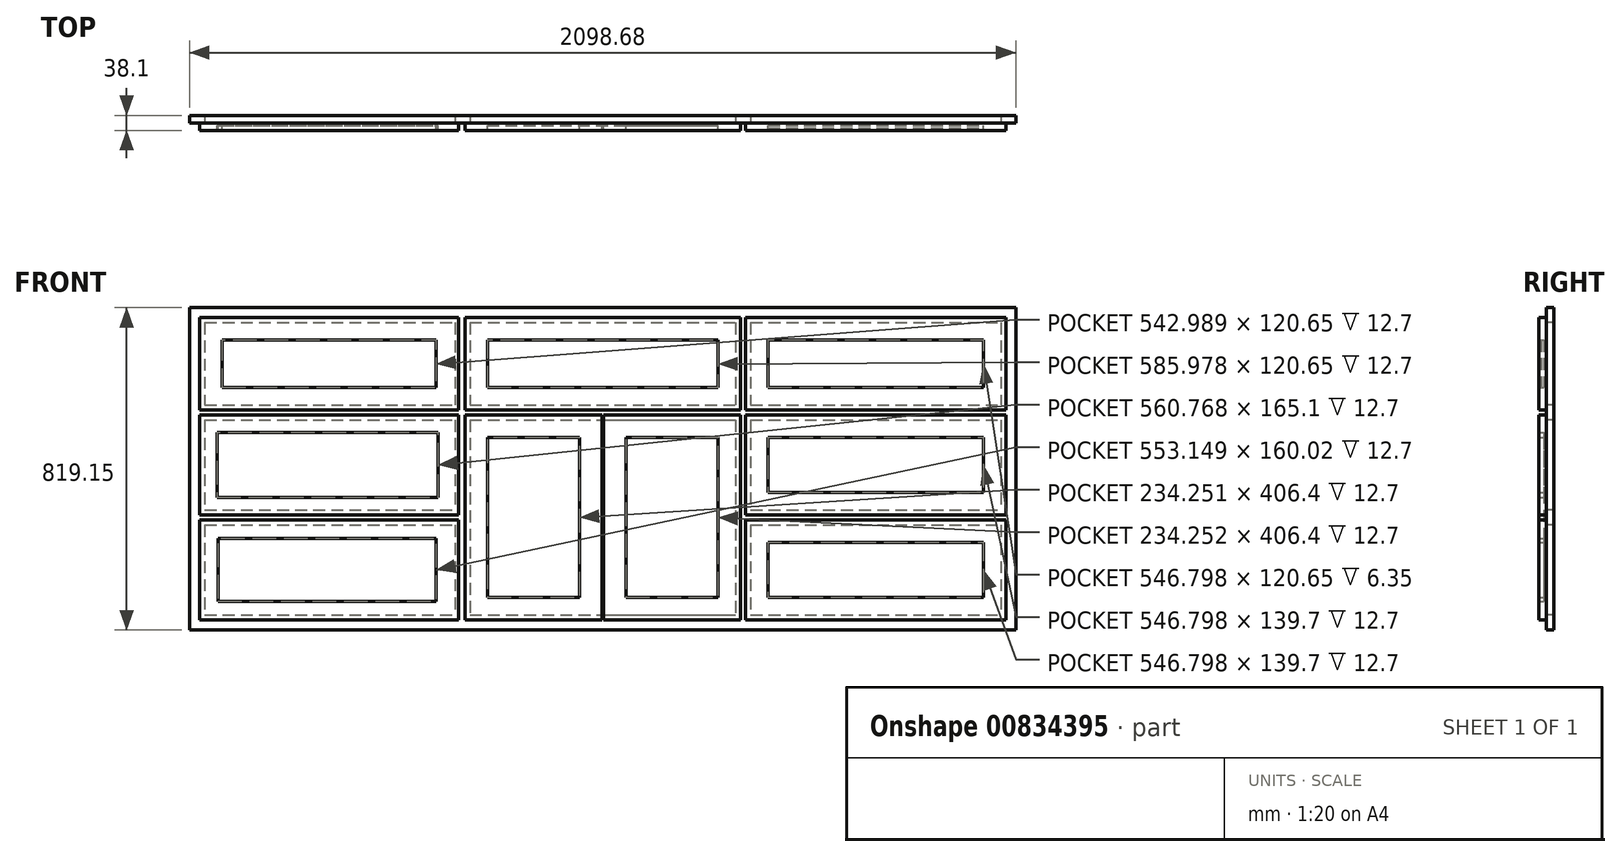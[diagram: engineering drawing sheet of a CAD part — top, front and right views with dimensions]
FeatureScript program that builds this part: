
annotation { "Feature Type Name" : "Feature", "Feature Type Description" : "" }
export const myFeature = defineFeature(function(context is Context, id is Id, definition is map)
    precondition{}
    {
        {
            var Q0;
            Q0=qCreatedBy(makeId("Front.planeOp"),FACE);
            var sketch = newSketch(context, id + "F0", { "sketchPlane" : qUnion([Q0])});
            skLineSegment(sketch, "E0.bottom", {"start": v(-1024.55, 548.46) * mm, "end": v(-350.75, 548.46) * mm});
            skLineSegment(sketch, "E0.left", {"start": v(-1024.55, 548.46) * mm, "end": v(-1024.55, -270.7) * mm});
            skLineSegment(sketch, "E0.right", {"start": v(1074.13, 548.46) * mm, "end": v(1074.13, -270.7) * mm});
            skLineSegment(sketch, "E1.0", {"start": v(-1024.55, -270.7) * mm, "end": v(-350.75, -270.7) * mm});
            skLineSegment(sketch, "E2", {"start": v(24.79, 721.9) * mm, "end": v(24.79, -476.43) * mm, "construction": true});
            skPoint(sketch, "E2.startSnap0", {"position": v(24.79, 548.46) * mm});
            skLineSegment(sketch, "E3.0", {"start": v(-986.45, -232.6) * mm, "end": v(-350.75, -232.6) * mm});
            skLineSegment(sketch, "E4.0", {"start": v(-986.45, 548.46) * mm, "end": v(-986.45, -270.7) * mm});
            skLineSegment(sketch, "E5.0", {"start": v(1036.03, 548.46) * mm, "end": v(1036.03, -270.7) * mm});
            skLineSegment(sketch, "E6.0", {"start": v(-986.45, 510.36) * mm, "end": v(-350.75, 510.36) * mm});
            skLineSegment(sketch, "E7", {"start": v(362.23, 548.46) * mm, "end": v(362.23, -270.7) * mm});
            skLineSegment(sketch, "E8.MirrorCS", {"start": v(-312.65, 548.46) * mm, "end": v(-312.65, -270.7) * mm});
            skLineSegment(sketch, "E9.0", {"start": v(400.33, 548.46) * mm, "end": v(400.33, -270.7) * mm});
            skLineSegment(sketch, "E10.0", {"start": v(-350.75, 548.46) * mm, "end": v(-350.75, -270.7) * mm});
            skLineSegment(sketch, "E11.trimOffspring", {"start": v(-312.65, 510.36) * mm, "end": v(362.23, 510.36) * mm});
            skLineSegment(sketch, "E12.trimOffspring", {"start": v(-312.65, 548.46) * mm, "end": v(362.23, 548.46) * mm});
            skLineSegment(sketch, "E13", {"start": v(-350.75, 548.46) * mm, "end": v(-312.65, 548.46) * mm});
            skLineSegment(sketch, "E14.trimOffspring", {"start": v(-312.65, -232.6) * mm, "end": v(362.23, -232.6) * mm});
            skLineSegment(sketch, "E15.trimOffspring", {"start": v(-312.65, -270.7) * mm, "end": v(362.23, -270.7) * mm});
            skLineSegment(sketch, "E16", {"start": v(-350.75, -270.7) * mm, "end": v(-312.65, -270.7) * mm});
            skLineSegment(sketch, "E17.trimOffspring", {"start": v(400.33, -232.6) * mm, "end": v(1036.03, -232.6) * mm});
            skLineSegment(sketch, "E18.trimOffspring", {"start": v(400.33, -270.7) * mm, "end": v(1074.13, -270.7) * mm});
            skLineSegment(sketch, "E19", {"start": v(362.23, -270.7) * mm, "end": v(400.33, -270.7) * mm});
            skLineSegment(sketch, "E20.trimOffspring", {"start": v(400.33, 548.46) * mm, "end": v(1074.13, 548.46) * mm});
            skLineSegment(sketch, "E21.trimOffspring", {"start": v(400.33, 510.36) * mm, "end": v(1036.03, 510.36) * mm});
            skLineSegment(sketch, "E22", {"start": v(362.23, 548.46) * mm, "end": v(400.33, 548.46) * mm});
            skLineSegment(sketch, "E23", {"start": v(-986.45, 138.88) * mm, "end": v(1036.03, 138.88) * mm, "construction": true});
            skLineSegment(sketch, "E24.0", {"start": v(-986.45, -4) * mm, "end": v(-350.75, -4) * mm});
            skLineSegment(sketch, "E25.0", {"start": v(400.33, -4) * mm, "end": v(1036.03, -4) * mm});
            skLineSegment(sketch, "E26.0", {"start": v(-986.45, 262.7) * mm, "end": v(-350.75, 262.7) * mm});
            skLineSegment(sketch, "E27.0", {"start": v(-986.45, 300.8) * mm, "end": v(-350.75, 300.8) * mm});
            skLineSegment(sketch, "E28", {"start": v(-986.45, 34.1) * mm, "end": v(-350.75, 34.1) * mm});
            skLineSegment(sketch, "E29", {"start": v(400.33, 34.1) * mm, "end": v(1036.03, 34.1) * mm});
            skLineSegment(sketch, "E30.bottom", {"start": v(-1024.55, -270.7) * mm, "end": v(1074.13, -270.7) * mm});
            skLineSegment(sketch, "E30.top", {"start": v(-1024.55, -346.9) * mm, "end": v(1074.13, -346.9) * mm});
            skLineSegment(sketch, "E30.left", {"start": v(-1024.55, -270.7) * mm, "end": v(-1024.55, -346.9) * mm});
            skLineSegment(sketch, "E30.right", {"start": v(1074.13, -270.7) * mm, "end": v(1074.13, -346.9) * mm});
            skLineSegment(sketch, "E31.trimOffspring", {"start": v(-312.65, 300.8) * mm, "end": v(362.23, 300.8) * mm});
            skLineSegment(sketch, "E32.trimOffspring", {"start": v(-312.65, 262.7) * mm, "end": v(362.23, 262.7) * mm});
            skLineSegment(sketch, "E33.trimOffspring", {"start": v(400.33, 300.8) * mm, "end": v(1036.03, 300.8) * mm});
            skLineSegment(sketch, "E34.trimOffspring", {"start": v(400.33, 262.7) * mm, "end": v(1036.03, 262.7) * mm});
            skSolve(sketch);
        }
        {
            var Q0;
            {var subQ3=sQuery(id+"F0.wireOp",EDGE,"E0.left");Q0=makeQuery(id+"F0.imprint","IMPRINT",FACE,{"disambiguationData":[TD([[makeQuery(id+"F0.imprint","IMPRINT",EDGE,{"derivedFrom":subQ3}),1.0]])]});}
            var Q1;
            {var subQ0=sQuery(id+"F0.wireOp",EDGE,"E3.0");Q1=makeQuery(id+"F0.imprint","IMPRINT",FACE,{"disambiguationData":[TD([[makeQuery(id+"F0.imprint","IMPRINT",EDGE,{"derivedFrom":subQ0}),-1.0]])]});}
            var Q2;
            {var subQ0=sQuery(id+"F0.wireOp",EDGE,"E24.0");Q2=makeQuery(id+"F0.imprint","IMPRINT",FACE,{"disambiguationData":[TD([[makeQuery(id+"F0.imprint","IMPRINT",EDGE,{"derivedFrom":subQ0}),1.0]])]});}
            var Q3;
            {var subQ0=sQuery(id+"F0.wireOp",EDGE,"E26.0");Q3=makeQuery(id+"F0.imprint","IMPRINT",FACE,{"disambiguationData":[TD([[makeQuery(id+"F0.imprint","IMPRINT",EDGE,{"derivedFrom":subQ0}),1.0]])]});}
            var Q4;
            {var subQ5=sQuery(id+"F0.wireOp",EDGE,"E6.0");Q4=makeQuery(id+"F0.imprint","IMPRINT",FACE,{"disambiguationData":[TD([[makeQuery(id+"F0.imprint","IMPRINT",EDGE,{"derivedFrom":subQ5}),1.0]])]});}
            var Q5;
            {var subQ8=sQuery(id+"F0.wireOp",EDGE,"E13");Q5=makeQuery(id+"F0.imprint","IMPRINT",FACE,{"disambiguationData":[TD([[makeQuery(id+"F0.imprint","IMPRINT",EDGE,{"derivedFrom":subQ8}),-1.0]])]});}
            var Q6;
            {var subQ2=sQuery(id+"F0.wireOp",EDGE,"E11.trimOffspring");Q6=makeQuery(id+"F0.imprint","IMPRINT",FACE,{"disambiguationData":[TD([[makeQuery(id+"F0.imprint","IMPRINT",EDGE,{"derivedFrom":subQ2}),1.0]])]});}
            var Q7;
            {var subQ0=sQuery(id+"F0.wireOp",EDGE,"E31.trimOffspring");Q7=makeQuery(id+"F0.imprint","IMPRINT",FACE,{"disambiguationData":[TD([[makeQuery(id+"F0.imprint","IMPRINT",EDGE,{"derivedFrom":subQ0}),-1.0]])]});}
            var Q8;
            {var subQ3=sQuery(id+"F0.wireOp",EDGE,"E14.trimOffspring");Q8=makeQuery(id+"F0.imprint","IMPRINT",FACE,{"disambiguationData":[TD([[makeQuery(id+"F0.imprint","IMPRINT",EDGE,{"derivedFrom":subQ3}),-1.0]])]});}
            var Q9;
            {var subQ0=sQuery(id+"F0.wireOp",EDGE,"E22");Q9=makeQuery(id+"F0.imprint","IMPRINT",FACE,{"disambiguationData":[TD([[makeQuery(id+"F0.imprint","IMPRINT",EDGE,{"derivedFrom":subQ0}),-1.0]])]});}
            var Q10;
            {var subQ0=sQuery(id+"F0.wireOp",EDGE,"E25.0");Q10=makeQuery(id+"F0.imprint","IMPRINT",FACE,{"disambiguationData":[TD([[makeQuery(id+"F0.imprint","IMPRINT",EDGE,{"derivedFrom":subQ0}),1.0]])]});}
            var Q11;
            {var subQ0=sQuery(id+"F0.wireOp",EDGE,"E33.trimOffspring");Q11=makeQuery(id+"F0.imprint","IMPRINT",FACE,{"disambiguationData":[TD([[makeQuery(id+"F0.imprint","IMPRINT",EDGE,{"derivedFrom":subQ0}),-1.0]])]});}
            var Q12;
            {var subQ3=sQuery(id+"F0.wireOp",EDGE,"E21.trimOffspring");Q12=makeQuery(id+"F0.imprint","IMPRINT",FACE,{"disambiguationData":[TD([[makeQuery(id+"F0.imprint","IMPRINT",EDGE,{"derivedFrom":subQ3}),1.0]])]});}
            var Q13;
            {var subQ3=sQuery(id+"F0.wireOp",EDGE,"E17.trimOffspring");Q13=makeQuery(id+"F0.imprint","IMPRINT",FACE,{"disambiguationData":[TD([[makeQuery(id+"F0.imprint","IMPRINT",EDGE,{"derivedFrom":subQ3}),-1.0]])]});}
            var Q14;
            {var subQ3=sQuery(id+"F0.wireOp",EDGE,"E0.right");Q14=makeQuery(id+"F0.imprint","IMPRINT",FACE,{"disambiguationData":[TD([[makeQuery(id+"F0.imprint","IMPRINT",EDGE,{"derivedFrom":subQ3}),-1.0]])]});}
            extrude(context, id + "F1", {"entities" : qUnion([Q0, Q1, Q2, Q3, Q4, Q5, Q6, Q7, Q8, Q9, Q10, Q11, Q12, Q13, Q14]), "oppositeDirection" : true, "depth" : 19.05 * mm, "offsetDistance" : 25.4 * mm});
        }
        {
            var Q0;
            {var subQ0=sQuery(id+"F0.wireOp",EDGE,"E14.trimOffspring");Q0=makeQuery(id+"F0.imprint","IMPRINT",FACE,{"disambiguationData":[TD([[makeQuery(id+"F0.imprint","IMPRINT",EDGE,{"derivedFrom":subQ0}),1.0]])]});}
            var sketch = newSketch(context, id + "F2", { "sketchPlane" : qUnion([Q0])});
            skLineSegment(sketch, "E35.0", {"start": v(-999.15, 523.06) * mm, "end": v(-999.15, 288.1) * mm});
            skLineSegment(sketch, "E36.0", {"start": v(-341.86, 523.06) * mm, "end": v(-341.86, 288.1) * mm});
            skLineSegment(sketch, "E37.0", {"start": v(-999.15, 523.06) * mm, "end": v(-341.86, 523.06) * mm});
            skLineSegment(sketch, "E38.0", {"start": v(-999.15, 288.1) * mm, "end": v(-341.86, 288.1) * mm});
            skLineSegment(sketch, "E39.0", {"start": v(-999.15, 275.4) * mm, "end": v(-341.86, 275.4) * mm});
            skLineSegment(sketch, "E40.0", {"start": v(-999.15, 21.4) * mm, "end": v(-341.86, 21.4) * mm});
            skLineSegment(sketch, "E41.0", {"start": v(-999.15, 8.7) * mm, "end": v(-341.86, 8.7) * mm});
            skLineSegment(sketch, "E42.0", {"start": v(-999.15, -245.3) * mm, "end": v(-341.86, -245.3) * mm});
            skLineSegment(sketch, "E43.0", {"start": v(-325.35, 275.4) * mm, "end": v(-325.35, -245.3) * mm});
            skLineSegment(sketch, "E44.0", {"start": v(374.93, 523.06) * mm, "end": v(374.93, 288.1) * mm});
            skLineSegment(sketch, "E45.0", {"start": v(-325.35, 288.1) * mm, "end": v(374.93, 288.1) * mm});
            skLineSegment(sketch, "E46.0", {"start": v(-325.35, 275.4) * mm, "end": v(23.2, 275.4) * mm});
            skLineSegment(sketch, "E47.0", {"start": v(-325.35, -245.3) * mm, "end": v(23.2, -245.3) * mm});
            skLineSegment(sketch, "E48.0", {"start": v(-325.35, 523.06) * mm, "end": v(374.93, 523.06) * mm});
            skLineSegment(sketch, "E49.0", {"start": v(387.63, 523.06) * mm, "end": v(1048.73, 523.06) * mm});
            skLineSegment(sketch, "E50.0", {"start": v(387.63, 523.06) * mm, "end": v(387.63, 288.1) * mm});
            skLineSegment(sketch, "E51.0", {"start": v(387.63, 288.1) * mm, "end": v(1048.73, 288.1) * mm});
            skLineSegment(sketch, "E52.0", {"start": v(387.63, 275.4) * mm, "end": v(1048.73, 275.4) * mm});
            skLineSegment(sketch, "E53.0", {"start": v(1048.73, 523.06) * mm, "end": v(1048.73, 288.1) * mm});
            skLineSegment(sketch, "E54.0", {"start": v(387.63, 21.4) * mm, "end": v(1048.73, 21.4) * mm});
            skLineSegment(sketch, "E55.0", {"start": v(387.63, 8.7) * mm, "end": v(1048.73, 8.7) * mm});
            skLineSegment(sketch, "E56.0", {"start": v(387.63, -245.3) * mm, "end": v(1048.73, -245.3) * mm});
            skLineSegment(sketch, "E57.trimOffspring", {"start": v(387.63, 275.4) * mm, "end": v(387.63, 21.4) * mm});
            skLineSegment(sketch, "E58.trimOffspring", {"start": v(374.93, 275.4) * mm, "end": v(374.93, -245.3) * mm});
            skLineSegment(sketch, "E59.trimOffspring", {"start": v(1048.73, 275.4) * mm, "end": v(1048.73, 21.4) * mm});
            skLineSegment(sketch, "E60.trimOffspring", {"start": v(387.63, 8.7) * mm, "end": v(387.63, -245.3) * mm});
            skLineSegment(sketch, "E61.trimOffspring", {"start": v(1048.73, 8.7) * mm, "end": v(1048.73, -245.3) * mm});
            skLineSegment(sketch, "E62.trimOffspring", {"start": v(-999.15, 275.4) * mm, "end": v(-999.15, 21.4) * mm});
            skLineSegment(sketch, "E63.trimOffspring", {"start": v(-999.15, 8.7) * mm, "end": v(-999.15, -245.3) * mm});
            skLineSegment(sketch, "E64.trimOffspring", {"start": v(-341.86, 8.7) * mm, "end": v(-341.86, -245.3) * mm});
            skLineSegment(sketch, "E65.trimOffspring", {"start": v(-341.86, 275.4) * mm, "end": v(-341.86, 21.4) * mm});
            skLineSegment(sketch, "E66", {"start": v(-325.35, 523.06) * mm, "end": v(-325.35, 288.1) * mm});
            skLineSegment(sketch, "E67.0", {"start": v(-942, 465.9) * mm, "end": v(-399.01, 465.9) * mm});
            skLineSegment(sketch, "E67.1", {"start": v(-942, 465.9) * mm, "end": v(-942, 345.26) * mm});
            skLineSegment(sketch, "E67.2", {"start": v(-942, 345.26) * mm, "end": v(-399.01, 345.26) * mm});
            skLineSegment(sketch, "E67.3", {"start": v(-399.01, 465.9) * mm, "end": v(-399.01, 345.26) * mm});
            skLineSegment(sketch, "E68.0", {"start": v(-954.7, 230.96) * mm, "end": v(-393.93, 230.96) * mm});
            skLineSegment(sketch, "E69.0", {"start": v(-393.93, 230.96) * mm, "end": v(-393.93, 65.86) * mm});
            skLineSegment(sketch, "E70.0", {"start": v(-954.7, 230.96) * mm, "end": v(-954.7, 65.86) * mm});
            skLineSegment(sketch, "E71.0", {"start": v(-954.7, 65.86) * mm, "end": v(-393.93, 65.86) * mm});
            skLineSegment(sketch, "E72.0", {"start": v(-952.16, -38.28) * mm, "end": v(-399.01, -38.28) * mm});
            skLineSegment(sketch, "E73.0", {"start": v(-399.01, -38.28) * mm, "end": v(-399.01, -198.3) * mm});
            skLineSegment(sketch, "E74.0", {"start": v(-952.16, -198.3) * mm, "end": v(-399.01, -198.3) * mm});
            skLineSegment(sketch, "E75.0", {"start": v(-952.16, -38.28) * mm, "end": v(-952.16, -198.3) * mm});
            skLineSegment(sketch, "E76.0", {"start": v(-964.86, -25.58) * mm, "end": v(-386.31, -25.58) * mm, "construction": true});
            skLineSegment(sketch, "E76.1", {"start": v(-964.86, -25.58) * mm, "end": v(-964.86, -211) * mm, "construction": true});
            skLineSegment(sketch, "E76.2", {"start": v(-964.86, -211) * mm, "end": v(-386.31, -211) * mm, "construction": true});
            skLineSegment(sketch, "E76.3", {"start": v(-386.31, -25.58) * mm, "end": v(-386.31, -211) * mm, "construction": true});
            skLineSegment(sketch, "E77.0", {"start": v(-967.4, 53.16) * mm, "end": v(-381.23, 53.16) * mm, "construction": true});
            skLineSegment(sketch, "E77.1", {"start": v(-967.4, 243.66) * mm, "end": v(-967.4, 53.16) * mm, "construction": true});
            skLineSegment(sketch, "E77.2", {"start": v(-967.4, 243.66) * mm, "end": v(-381.23, 243.66) * mm, "construction": true});
            skLineSegment(sketch, "E77.3", {"start": v(-381.23, 243.66) * mm, "end": v(-381.23, 53.16) * mm, "construction": true});
            skLineSegment(sketch, "E78.0", {"start": v(-954.7, 478.6) * mm, "end": v(-954.7, 332.56) * mm, "construction": true});
            skLineSegment(sketch, "E78.1", {"start": v(-954.7, 478.6) * mm, "end": v(-386.31, 478.6) * mm, "construction": true});
            skLineSegment(sketch, "E78.2", {"start": v(-386.31, 478.6) * mm, "end": v(-386.31, 332.56) * mm, "construction": true});
            skLineSegment(sketch, "E78.3", {"start": v(-954.7, 332.56) * mm, "end": v(-386.31, 332.56) * mm, "construction": true});
            skLineSegment(sketch, "E79.0", {"start": v(23.2, 275.4) * mm, "end": v(23.2, -245.3) * mm});
            skLineSegment(sketch, "E80.0", {"start": v(26.38, 275.4) * mm, "end": v(26.38, -245.3) * mm});
            skLineSegment(sketch, "E81.trimOffspring", {"start": v(26.38, 275.4) * mm, "end": v(374.93, 275.4) * mm});
            skLineSegment(sketch, "E82.trimOffspring", {"start": v(26.38, -245.3) * mm, "end": v(374.93, -245.3) * mm});
            skLineSegment(sketch, "E83.0", {"start": v(-268.2, 465.9) * mm, "end": v(-268.2, 345.26) * mm});
            skLineSegment(sketch, "E84.0", {"start": v(-268.2, 465.9) * mm, "end": v(317.78, 465.9) * mm});
            skLineSegment(sketch, "E85.0", {"start": v(317.78, 465.9) * mm, "end": v(317.78, 345.26) * mm});
            skLineSegment(sketch, "E86.0", {"start": v(-268.2, 345.26) * mm, "end": v(317.78, 345.26) * mm});
            skLineSegment(sketch, "E87.0", {"start": v(-268.2, 218.26) * mm, "end": v(-33.95, 218.26) * mm});
            skLineSegment(sketch, "E88.0", {"start": v(-33.95, 218.26) * mm, "end": v(-33.95, -188.14) * mm});
            skLineSegment(sketch, "E89.0", {"start": v(-268.2, -188.14) * mm, "end": v(-33.95, -188.14) * mm});
            skLineSegment(sketch, "E90.0", {"start": v(-268.2, 218.26) * mm, "end": v(-268.2, -188.14) * mm});
            skLineSegment(sketch, "E91.0", {"start": v(83.53, 218.26) * mm, "end": v(83.53, -188.14) * mm});
            skLineSegment(sketch, "E92.0", {"start": v(83.53, 218.26) * mm, "end": v(317.78, 218.26) * mm});
            skLineSegment(sketch, "E93.0", {"start": v(317.78, 218.26) * mm, "end": v(317.78, -188.14) * mm});
            skLineSegment(sketch, "E94.0", {"start": v(83.53, -188.14) * mm, "end": v(317.78, -188.14) * mm});
            skLineSegment(sketch, "E95.0", {"start": v(444.78, 465.9) * mm, "end": v(444.78, 345.26) * mm});
            skLineSegment(sketch, "E96.0", {"start": v(444.78, 218.26) * mm, "end": v(444.78, 78.56) * mm});
            skLineSegment(sketch, "E97.0", {"start": v(444.78, -48.44) * mm, "end": v(444.78, -188.14) * mm});
            skLineSegment(sketch, "E98.0", {"start": v(444.78, 465.9) * mm, "end": v(991.58, 465.9) * mm});
            skLineSegment(sketch, "E99.0", {"start": v(991.58, 465.9) * mm, "end": v(991.58, 345.26) * mm});
            skLineSegment(sketch, "E100.0", {"start": v(991.58, 218.26) * mm, "end": v(991.58, 78.56) * mm});
            skLineSegment(sketch, "E101.0", {"start": v(991.58, -48.44) * mm, "end": v(991.58, -188.14) * mm});
            skLineSegment(sketch, "E102.0", {"start": v(444.78, 345.26) * mm, "end": v(991.58, 345.26) * mm});
            skLineSegment(sketch, "E103.0", {"start": v(444.78, 218.26) * mm, "end": v(991.58, 218.26) * mm});
            skLineSegment(sketch, "E104.0", {"start": v(444.78, 78.56) * mm, "end": v(991.58, 78.56) * mm});
            skLineSegment(sketch, "E105.0", {"start": v(444.78, -48.44) * mm, "end": v(991.58, -48.44) * mm});
            skLineSegment(sketch, "E106.0", {"start": v(444.78, -188.14) * mm, "end": v(991.58, -188.14) * mm});
            skSolve(sketch);
        }
        {
            var Q0;
            Q0=makeQuery(id+"F2.imprint","IMPRINT",FACE,{"disambiguationData":[TD([[makeQuery(id+"F2.imprint","IMPRINT",EDGE,{"derivedFrom":sQuery(id+"F2.wireOp",EDGE,"E41.0")}),-1.0]])]});
            extrude(context, id + "F3", {"entities" : qUnion([Q0]), "operationType" : NewBodyOperationType.ADD, "depth" : 19.05 * mm, "offsetDistance" : 25.4 * mm});
        }
        {
            var Q0;
            Q0=makeQuery(id+"F2.imprint","IMPRINT",FACE,{"disambiguationData":[TD([[makeQuery(id+"F2.imprint","IMPRINT",EDGE,{"derivedFrom":sQuery(id+"F2.wireOp",EDGE,"E39.0")}),-1.0]])]});
            extrude(context, id + "F4", {"entities" : qUnion([Q0]), "operationType" : NewBodyOperationType.ADD, "depth" : 19.05 * mm, "offsetDistance" : 25.4 * mm});
        }
        {
            var Q0;
            Q0=makeQuery(id+"F2.imprint","IMPRINT",FACE,{"disambiguationData":[TD([[makeQuery(id+"F2.imprint","IMPRINT",EDGE,{"derivedFrom":sQuery(id+"F2.wireOp",EDGE,"E35.0")}),1.0]])]});
            extrude(context, id + "F5", {"entities" : qUnion([Q0]), "operationType" : NewBodyOperationType.ADD, "depth" : 19.05 * mm, "offsetDistance" : 25.4 * mm});
        }
        {
            var Q0;
            Q0=makeQuery(id+"F2.imprint","IMPRINT",FACE,{"disambiguationData":[TD([[makeQuery(id+"F2.imprint","IMPRINT",EDGE,{"derivedFrom":sQuery(id+"F2.wireOp",EDGE,"E67.0")}),-1.0]])]});
            extrude(context, id + "F6", {"entities" : qUnion([Q0]), "operationType" : NewBodyOperationType.ADD, "depth" : 6.35 * mm, "offsetDistance" : 25.4 * mm});
        }
        {
            var Q0;
            Q0=makeQuery(id+"F2.imprint","IMPRINT",FACE,{"disambiguationData":[TD([[makeQuery(id+"F2.imprint","IMPRINT",EDGE,{"derivedFrom":sQuery(id+"F2.wireOp",EDGE,"E44.0")}),-1.0]])]});
            extrude(context, id + "F7", {"entities" : qUnion([Q0]), "operationType" : NewBodyOperationType.ADD, "depth" : 19.05 * mm, "offsetDistance" : 25.4 * mm});
        }
        {
            var Q0;
            Q0=makeQuery(id+"F2.imprint","IMPRINT",FACE,{"disambiguationData":[TD([[makeQuery(id+"F2.imprint","IMPRINT",EDGE,{"derivedFrom":sQuery(id+"F2.wireOp",EDGE,"E83.0")}),1.0]])]});
            extrude(context, id + "F8", {"entities" : qUnion([Q0]), "operationType" : NewBodyOperationType.ADD, "depth" : 6.35 * mm, "offsetDistance" : 25.4 * mm});
        }
        {
            var Q0;
            Q0=makeQuery(id+"F2.imprint","IMPRINT",FACE,{"disambiguationData":[TD([[makeQuery(id+"F2.imprint","IMPRINT",EDGE,{"derivedFrom":sQuery(id+"F2.wireOp",EDGE,"E68.0")}),-1.0]])]});
            var Q1;
            Q1=makeQuery(id+"F2.imprint","IMPRINT",FACE,{"disambiguationData":[TD([[makeQuery(id+"F2.imprint","IMPRINT",EDGE,{"derivedFrom":sQuery(id+"F2.wireOp",EDGE,"E72.0")}),-1.0]])]});
            extrude(context, id + "F9", {"entities" : qUnion([Q0, Q1]), "operationType" : NewBodyOperationType.ADD, "depth" : 6.35 * mm, "offsetDistance" : 25.4 * mm});
        }
        {
            var Q0;
            Q0=makeQuery(id+"F2.imprint","IMPRINT",FACE,{"disambiguationData":[TD([[makeQuery(id+"F2.imprint","IMPRINT",EDGE,{"derivedFrom":sQuery(id+"F2.wireOp",EDGE,"E43.0")}),1.0]])]});
            var Q1;
            Q1=makeQuery(id+"F2.imprint","IMPRINT",FACE,{"disambiguationData":[TD([[makeQuery(id+"F2.imprint","IMPRINT",EDGE,{"derivedFrom":sQuery(id+"F2.wireOp",EDGE,"E87.0")}),1.0]])]});
            var Q2;
            Q2=makeQuery(id+"F2.imprint","IMPRINT",FACE,{"disambiguationData":[TD([[makeQuery(id+"F2.imprint","IMPRINT",EDGE,{"derivedFrom":sQuery(id+"F2.wireOp",EDGE,"E58.trimOffspring")}),-1.0]])]});
            var Q3;
            Q3=makeQuery(id+"F2.imprint","IMPRINT",FACE,{"disambiguationData":[TD([[makeQuery(id+"F2.imprint","IMPRINT",EDGE,{"derivedFrom":sQuery(id+"F2.wireOp",EDGE,"E91.0")}),-1.0]])]});
            extrude(context, id + "F10", {"entities" : qUnion([Q0, Q1, Q2, Q3]), "operationType" : NewBodyOperationType.ADD, "depth" : 19.05 * mm, "offsetDistance" : 25.4 * mm});
        }
        {
            var Q0;
            Q0=makeQuery(id+"F2.imprint","IMPRINT",FACE,{"disambiguationData":[TD([[makeQuery(id+"F2.imprint","IMPRINT",EDGE,{"derivedFrom":sQuery(id+"F2.wireOp",EDGE,"E87.0")}),-1.0]])]});
            var Q1;
            Q1=makeQuery(id+"F2.imprint","IMPRINT",FACE,{"disambiguationData":[TD([[makeQuery(id+"F2.imprint","IMPRINT",EDGE,{"derivedFrom":sQuery(id+"F2.wireOp",EDGE,"E91.0")}),1.0]])]});
            extrude(context, id + "F11", {"entities" : qUnion([Q0, Q1]), "operationType" : NewBodyOperationType.ADD, "depth" : 6.35 * mm, "offsetDistance" : 25.4 * mm});
        }
        {
            var Q0;
            Q0=makeQuery(id+"F2.imprint","IMPRINT",FACE,{"disambiguationData":[TD([[makeQuery(id+"F2.imprint","IMPRINT",EDGE,{"derivedFrom":sQuery(id+"F2.wireOp",EDGE,"E49.0")}),-1.0]])]});
            var Q1;
            Q1=makeQuery(id+"F2.imprint","IMPRINT",FACE,{"disambiguationData":[TD([[makeQuery(id+"F2.imprint","IMPRINT",EDGE,{"derivedFrom":sQuery(id+"F2.wireOp",EDGE,"E52.0")}),-1.0]])]});
            var Q2;
            Q2=makeQuery(id+"F2.imprint","IMPRINT",FACE,{"disambiguationData":[TD([[makeQuery(id+"F2.imprint","IMPRINT",EDGE,{"derivedFrom":sQuery(id+"F2.wireOp",EDGE,"E55.0")}),-1.0]])]});
            extrude(context, id + "F12", {"entities" : qUnion([Q0, Q1, Q2]), "operationType" : NewBodyOperationType.ADD, "depth" : 19.05 * mm, "offsetDistance" : 25.4 * mm});
        }
        {
            var Q0;
            Q0=makeQuery(id+"F2.imprint","IMPRINT",FACE,{"disambiguationData":[TD([[makeQuery(id+"F2.imprint","IMPRINT",EDGE,{"derivedFrom":sQuery(id+"F2.wireOp",EDGE,"E95.0")}),1.0]])]});
            extrude(context, id + "F13", {"entities" : qUnion([Q0]), "operationType" : NewBodyOperationType.ADD, "depth" : 12.7 * mm, "offsetDistance" : 25.4 * mm});
        }
        {
            var Q0;
            Q0=makeQuery(id+"F13.opExtrude","CAP_FACE",FACE,{"disambiguationData":[OSD([sQuery(id+"F2.wireOp",EDGE,"E95.0"),sQuery(id+"F2.wireOp",EDGE,"E98.0"),sQuery(id+"F2.wireOp",EDGE,"E99.0"),sQuery(id+"F2.wireOp",EDGE,"E102.0")])],"isStart":false});
            extrude(context, id + "F14", {"entities" : qUnion([Q0]), "operationType" : NewBodyOperationType.REMOVE, "depth" : 6.35 * mm, "offsetDistance" : 25.4 * mm});
        }
        {
            var Q0;
            Q0=makeQuery(id+"F2.imprint","IMPRINT",FACE,{"disambiguationData":[TD([[makeQuery(id+"F2.imprint","IMPRINT",EDGE,{"derivedFrom":sQuery(id+"F2.wireOp",EDGE,"E95.0")}),1.0]])]});
            extrude(context, id + "F15", {"entities" : qUnion([Q0]), "operationType" : NewBodyOperationType.REMOVE, "oppositeDirection" : true, "depth" : 6.35 * mm, "offsetDistance" : 25.4 * mm});
        }
        {
            var Q0;
            Q0=makeQuery(id+"F2.imprint","IMPRINT",FACE,{"disambiguationData":[TD([[makeQuery(id+"F2.imprint","IMPRINT",EDGE,{"derivedFrom":sQuery(id+"F2.wireOp",EDGE,"E96.0")}),1.0]])]});
            var Q1;
            Q1=makeQuery(id+"F2.imprint","IMPRINT",FACE,{"disambiguationData":[TD([[makeQuery(id+"F2.imprint","IMPRINT",EDGE,{"derivedFrom":sQuery(id+"F2.wireOp",EDGE,"E97.0")}),1.0]])]});
            extrude(context, id + "F16", {"entities" : qUnion([Q0, Q1]), "operationType" : NewBodyOperationType.ADD, "depth" : 6.35 * mm, "offsetDistance" : 25.4 * mm});
        }
    });
